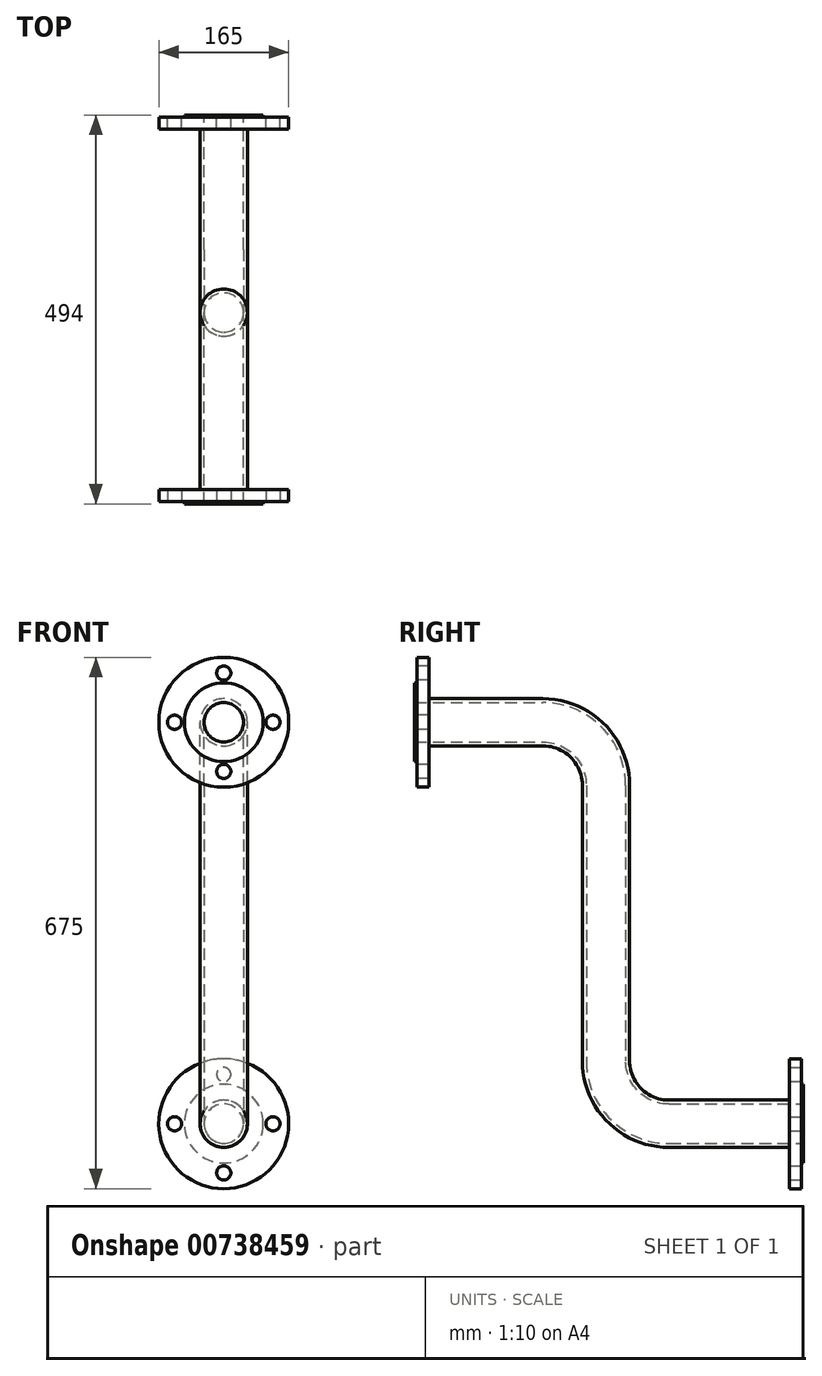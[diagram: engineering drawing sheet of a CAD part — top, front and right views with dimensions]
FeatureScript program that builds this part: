
annotation { "Feature Type Name" : "Feature", "Feature Type Description" : "" }
export const myFeature = defineFeature(function(context is Context, id is Id, definition is map)
    precondition{}
    {
        {
            var Q0;
            Q0=qCreatedBy(makeId("Right.planeOp"),FACE);
            var sketch = newSketch(context, id + "F0", { "sketchPlane" : qUnion([Q0])});
            skLineSegment(sketch, "E0", {"start": v(0, 0) * mm, "end": v(160, 0) * mm});
            skLineSegment(sketch, "E1", {"start": v(240, -80) * mm, "end": v(240, -430) * mm});
            skLineSegment(sketch, "E2", {"start": v(320, -510) * mm, "end": v(488, -510) * mm});
            skPoint(sketch, "E3.visualSharp", {"position": v(240, 0) * mm});
            skArc(sketch, "E3.filletArc", {"start": v(240, -80) * mm, "mid": v(216.57, -23.43) * mm, "end": v(160, 0) * mm});
            skPoint(sketch, "E4.visualSharp", {"position": v(240, -510) * mm});
            skArc(sketch, "E4.filletArc", {"start": v(240, -430) * mm, "mid": v(263.43, -486.57) * mm, "end": v(320, -510) * mm});
            skSolve(sketch);
        }
        {
            var Q0;
            Q0=qCreatedBy(makeId("Front.planeOp"),FACE);
            var sketch = newSketch(context, id + "F1", { "sketchPlane" : qUnion([Q0])});
            skCircle(sketch, "E5", {"center": v(0, 0) * mm, "radius": 25 * mm});
            skCircle(sketch, "E6", {"center": v(0, 0) * mm, "radius": 82.5 * mm});
            skCircle(sketch, "E7", {"center": v(0, 62.5) * mm, "radius": 9 * mm});
            skCircle(sketch, "E8.1.0", {"center": v(-62.5, 0) * mm, "radius": 9 * mm});
            skCircle(sketch, "E8.2.0", {"center": v(0, -62.5) * mm, "radius": 9 * mm});
            skCircle(sketch, "E8.3.0", {"center": v(62.5, 0) * mm, "radius": 9 * mm});
            skCircle(sketch, "E9", {"center": v(0, 0) * mm, "radius": 30 * mm});
            skSolve(sketch);
        }
        {
            var Q0;
            Q0=makeQuery(id+"F1.imprint","IMPRINT",FACE,{"disambiguationData":[TD([[makeQuery(id+"F1.imprint","IMPRINT",EDGE,{"derivedFrom":sQuery(id+"F1.wireOp",EDGE,"E5")}),-1.0]])]});
            var Q1;
            Q1=sQuery(id+"F0.wireOp",EDGE,"E0");
            var Q2;
            Q2=sQuery(id+"F0.wireOp",EDGE,"E3.filletArc");
            var Q3;
            Q3=sQuery(id+"F0.wireOp",EDGE,"E1");
            var Q4;
            Q4=sQuery(id+"F0.wireOp",EDGE,"E4.filletArc");
            var Q5;
            Q5=sQuery(id+"F0.wireOp",EDGE,"E2");
            sweep(context, id + "F2", {"profiles" : qUnion([Q0]), "path" : qUnion([Q1, Q2, Q3, Q4, Q5])});
        }
        {
            var Q0;
            Q0=makeQuery(id+"F1.imprint","IMPRINT",FACE,{"disambiguationData":[TD([[makeQuery(id+"F1.imprint","IMPRINT",EDGE,{"derivedFrom":sQuery(id+"F1.wireOp",EDGE,"E6")}),1.0]])]});
            extrude(context, id + "F3", {"entities" : qUnion([Q0]), "operationType" : NewBodyOperationType.ADD, "oppositeDirection" : true, "depth" : 15 * mm, "offsetDistance" : 25 * mm});
        }
        {
            var Q0;
            Q0=makeQuery(id+"F1.imprint","IMPRINT",FACE,{"disambiguationData":[TD([[makeQuery(id+"F1.imprint","IMPRINT",EDGE,{"derivedFrom":sQuery(id+"F1.wireOp",EDGE,"E6")}),1.0]])]});
            var sketch = newSketch(context, id + "F4", { "sketchPlane" : qUnion([Q0])});
            skCircle(sketch, "E10", {"center": v(0, 0) * mm, "radius": 50 * mm});
            skCircle(sketch, "E11.0", {"center": v(0, 0) * mm, "radius": 25 * mm});
            skSolve(sketch);
        }
        {
            var Q0;
            Q0 = qSketchRegion(id + "F4", true);
            extrude(context, id + "F5", {"entities" : qUnion([Q0]), "operationType" : NewBodyOperationType.ADD, "depth" : 3 * mm, "offsetDistance" : 25 * mm});
        }
        {
            var Q0;
            Q0=makeQuery(id+"F2.opSweep","CAP_FACE",FACE,{"disambiguationData":[OSD([sQuery(id+"F0.wireOp",VERTEX,"E2.end"),sQuery(id+"F1.wireOp",EDGE,"E5"),sQuery(id+"F1.wireOp",EDGE,"E9")])],"isStart":false});
            var sketch = newSketch(context, id + "F6", { "sketchPlane" : qUnion([Q0])});
            skCircle(sketch, "E12", {"center": v(0, -510) * mm, "radius": 82.5 * mm});
            skCircle(sketch, "E13", {"center": v(0, -447.5) * mm, "radius": 9 * mm});
            skCircle(sketch, "E14.1.0", {"center": v(-62.5, -510) * mm, "radius": 9 * mm});
            skCircle(sketch, "E14.2.0", {"center": v(0, -572.5) * mm, "radius": 9 * mm});
            skCircle(sketch, "E14.3.0", {"center": v(62.5, -510) * mm, "radius": 9 * mm});
            skSolve(sketch);
        }
        {
            var Q0;
            Q0=makeQuery(id+"F6.imprint","IMPRINT",FACE,{"disambiguationData":[TD([[makeQuery(id+"F6.imprint","IMPRINT",EDGE,{"derivedFrom":sQuery(id+"F6.wireOp",EDGE,"E12")}),1.0]])]});
            var Q1;
            {var subQ0=sQuery(id+"F0.wireOp",VERTEX,"E2.end");Q1=makeQuery(id+"F6.imprint","IMPRINT",FACE,{"disambiguationData":[TD([[makeQuery(id+"F6.imprint","IMPRINT",EDGE,{"derivedFrom":makeQuery(id+"F2.opSweep","CAP_EDGE",EDGE,{"disambiguationData":[OSD([subQ0,sQuery(id+"F1.wireOp",EDGE,"E5")])],"isStart":false})}),1.0]])]});}
            extrude(context, id + "F7", {"entities" : qUnion([Q0, Q1]), "operationType" : NewBodyOperationType.ADD, "oppositeDirection" : true, "depth" : 15 * mm, "offsetDistance" : 25 * mm});
        }
        {
            var Q0;
            {var subQ0=sQuery(id+"F1.wireOp",EDGE,"E5");var subQ1=sQuery(id+"F0.wireOp",VERTEX,"E2.end");Q0=makeQuery(id+"F7.boolean.opBoolean","MERGE",FACE,{"derivedFrom":[makeQuery(id+"F2.opSweep","CAP_FACE",FACE,{"disambiguationData":[OSD([subQ1,subQ0,sQuery(id+"F1.wireOp",EDGE,"E9")])],"isStart":false}),makeQuery(id+"F7.opExtrude","CAP_FACE",FACE,{"disambiguationData":[OSD([subQ1,subQ0,sQuery(id+"F6.wireOp",EDGE,"E12"),sQuery(id+"F6.wireOp",EDGE,"E13"),sQuery(id+"F6.wireOp",EDGE,"E14.1.0"),sQuery(id+"F6.wireOp",EDGE,"E14.2.0"),sQuery(id+"F6.wireOp",EDGE,"E14.3.0")])],"isStart":true})]});}
            var sketch = newSketch(context, id + "F8", { "sketchPlane" : qUnion([Q0])});
            skCircle(sketch, "E15", {"center": v(0, -510) * mm, "radius": 50 * mm});
            skSolve(sketch);
        }
        {
            var Q0;
            Q0=makeQuery(id+"F8.imprint","IMPRINT",FACE,{"disambiguationData":[TD([[makeQuery(id+"F8.imprint","IMPRINT",EDGE,{"derivedFrom":sQuery(id+"F8.wireOp",EDGE,"E15")}),1.0]])]});
            extrude(context, id + "F9", {"entities" : qUnion([Q0]), "operationType" : NewBodyOperationType.ADD, "depth" : 3 * mm, "offsetDistance" : 25 * mm});
        }
    });
